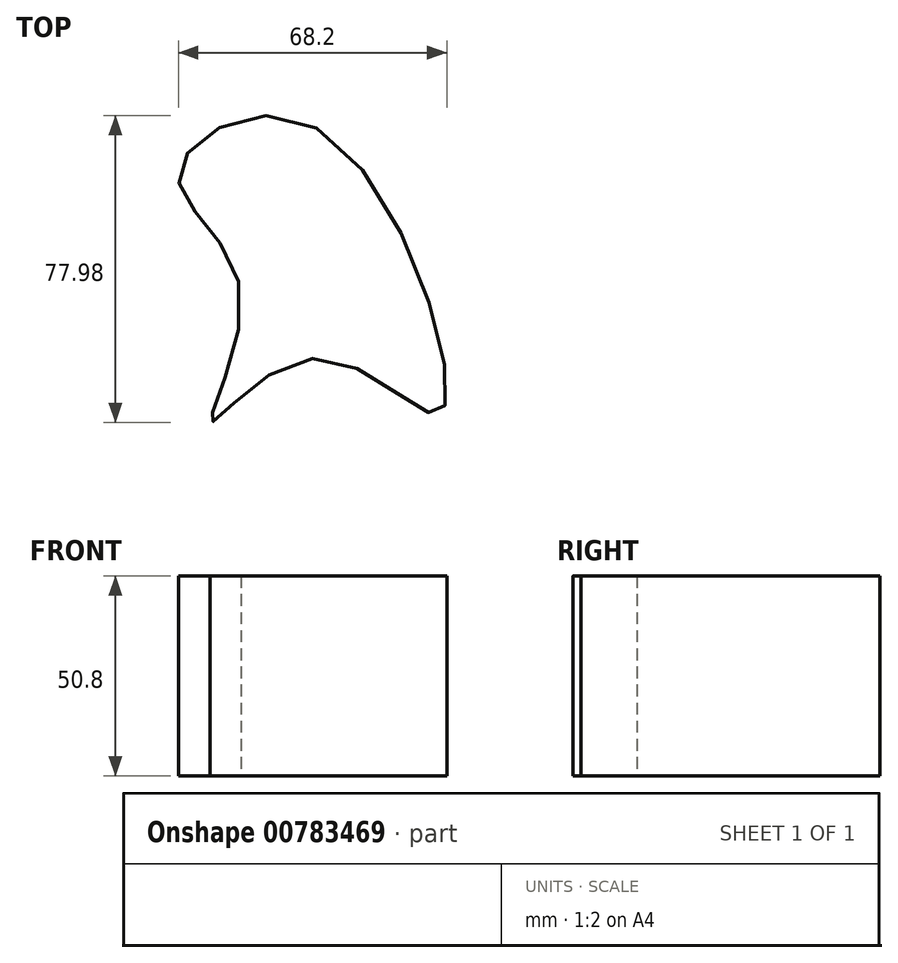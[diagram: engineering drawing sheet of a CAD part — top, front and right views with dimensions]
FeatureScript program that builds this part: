
annotation { "Feature Type Name" : "Feature", "Feature Type Description" : "" }
export const myFeature = defineFeature(function(context is Context, id is Id, definition is map)
    precondition{}
    {
        {
            var Q0;
            Q0=qCreatedBy(makeId("Top.planeOp"),FACE);
            var sketch = newSketch(context, id + "F0", { "sketchPlane" : qUnion([Q0])});
            skFitSpline(sketch, "E0", {"points": [v(0, 40.57) * mm, v(-35.01, 29.09) * mm, v(-19.45, 0) * mm, v(-26.86, -34.27) * mm, v(0, -17.97) * mm, v(31.68, -31.68) * mm, v(0, 40.57) * mm]});
            skSolve(sketch);
        }
        {
            var Q0;
            Q0 = qSketchRegion(id + "F0", true);
            extrude(context, id + "F1", {"entities" : qUnion([Q0]), "depth" : 50.8 * mm, "offsetDistance" : 25.4 * mm});
        }
    });
